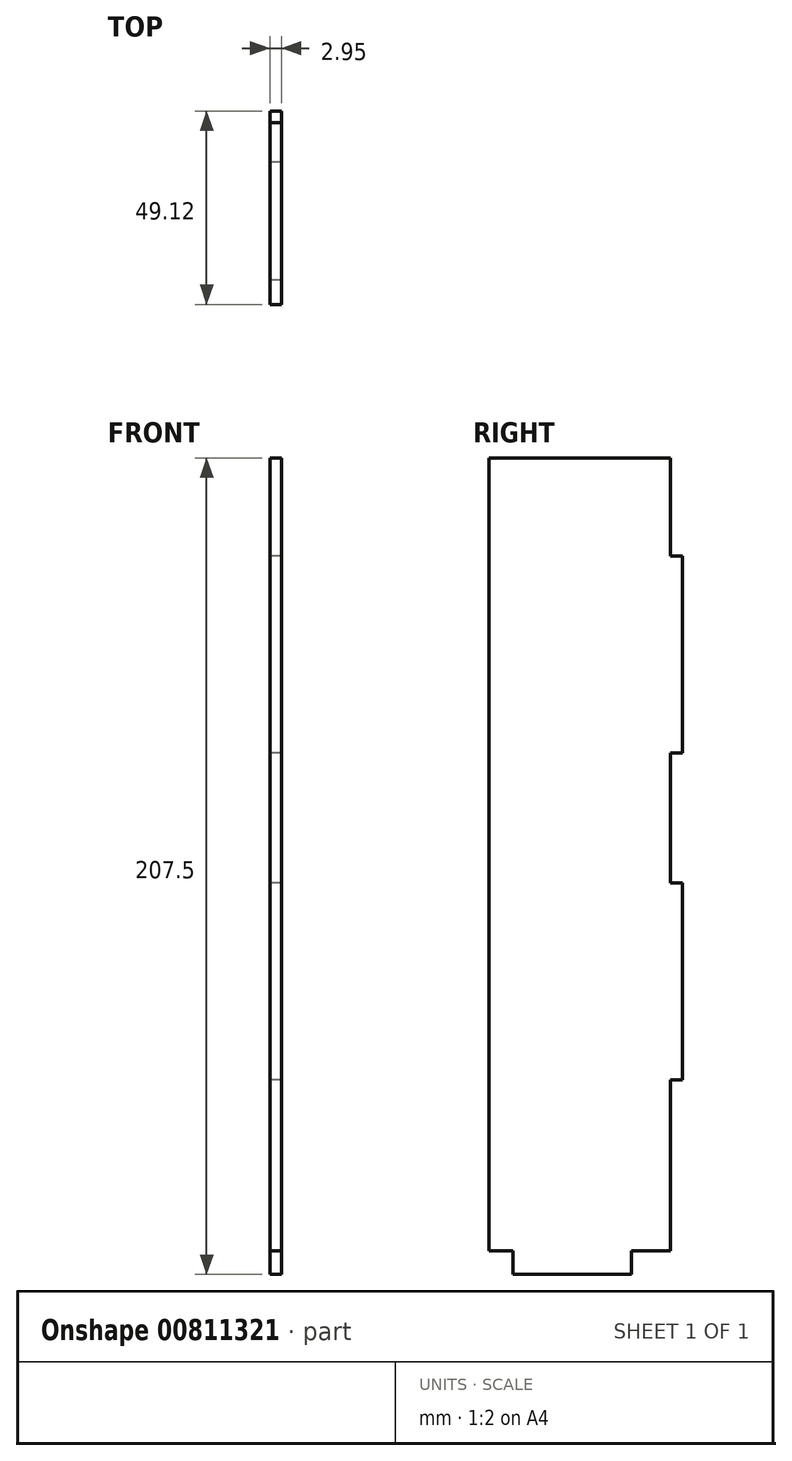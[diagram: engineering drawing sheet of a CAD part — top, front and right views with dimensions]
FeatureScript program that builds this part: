
annotation { "Feature Type Name" : "Feature", "Feature Type Description" : "" }
export const myFeature = defineFeature(function(context is Context, id is Id, definition is map)
    precondition{}
    {
        {
            var Q0;
            Q0=qCreatedBy(makeId("Right.planeOp"),FACE);
            var sketch = newSketch(context, id + "F0", { "sketchPlane" : qUnion([Q0])});
            skLineSegment(sketch, "E0.bottom", {"start": v(0, 8.05) * mm, "end": v(6.13, 8.05) * mm});
            skLineSegment(sketch, "E0.top", {"start": v(0, 209.55) * mm, "end": v(46.12, 209.55) * mm});
            skLineSegment(sketch, "E0.left", {"start": v(0, 8.05) * mm, "end": v(0, 209.55) * mm});
            skLineSegment(sketch, "E0.right", {"start": v(46.13, 8.05) * mm, "end": v(46.12, 51.55) * mm});
            skLineSegment(sketch, "E1.top", {"start": v(6.13, 2.05) * mm, "end": v(36.13, 2.05) * mm});
            skLineSegment(sketch, "E1.left", {"start": v(6.13, 8.05) * mm, "end": v(6.13, 2.05) * mm});
            skLineSegment(sketch, "E1.right", {"start": v(36.12, 8.05) * mm, "end": v(36.12, 2.05) * mm});
            skLineSegment(sketch, "E2", {"start": v(46.12, 8.05) * mm, "end": v(36.12, 8.05) * mm});
            skLineSegment(sketch, "E3.bottom", {"start": v(46.12, 184.55) * mm, "end": v(49.12, 184.55) * mm});
            skLineSegment(sketch, "E3.top", {"start": v(46.12, 134.55) * mm, "end": v(49.12, 134.55) * mm});
            skLineSegment(sketch, "E3.right", {"start": v(49.12, 184.55) * mm, "end": v(49.12, 134.55) * mm});
            skLineSegment(sketch, "E4.bottom", {"start": v(46.12, 101.55) * mm, "end": v(49.12, 101.55) * mm});
            skLineSegment(sketch, "E4.top", {"start": v(46.12, 51.55) * mm, "end": v(49.12, 51.55) * mm});
            skLineSegment(sketch, "E4.right", {"start": v(49.12, 101.55) * mm, "end": v(49.12, 51.55) * mm});
            skLineSegment(sketch, "E5.trimOffspring", {"start": v(46.12, 101.55) * mm, "end": v(46.12, 134.55) * mm});
            skLineSegment(sketch, "E6", {"start": v(46.12, 209.55) * mm, "end": v(46.12, 184.55) * mm});
            skSolve(sketch);
        }
        {
            var Q0;
            Q0=makeQuery(id+"F0.imprint","IMPRINT",FACE,{"disambiguationData":[TD([[makeQuery(id+"F0.imprint","IMPRINT",EDGE,{"derivedFrom":sQuery(id+"F0.wireOp",EDGE,"E0.bottom")}),1.0]])]});
            extrude(context, id + "F1", {"entities" : qUnion([Q0]), "depth" : 2.95 * mm, "offsetDistance" : 25 * mm});
        }
    });
